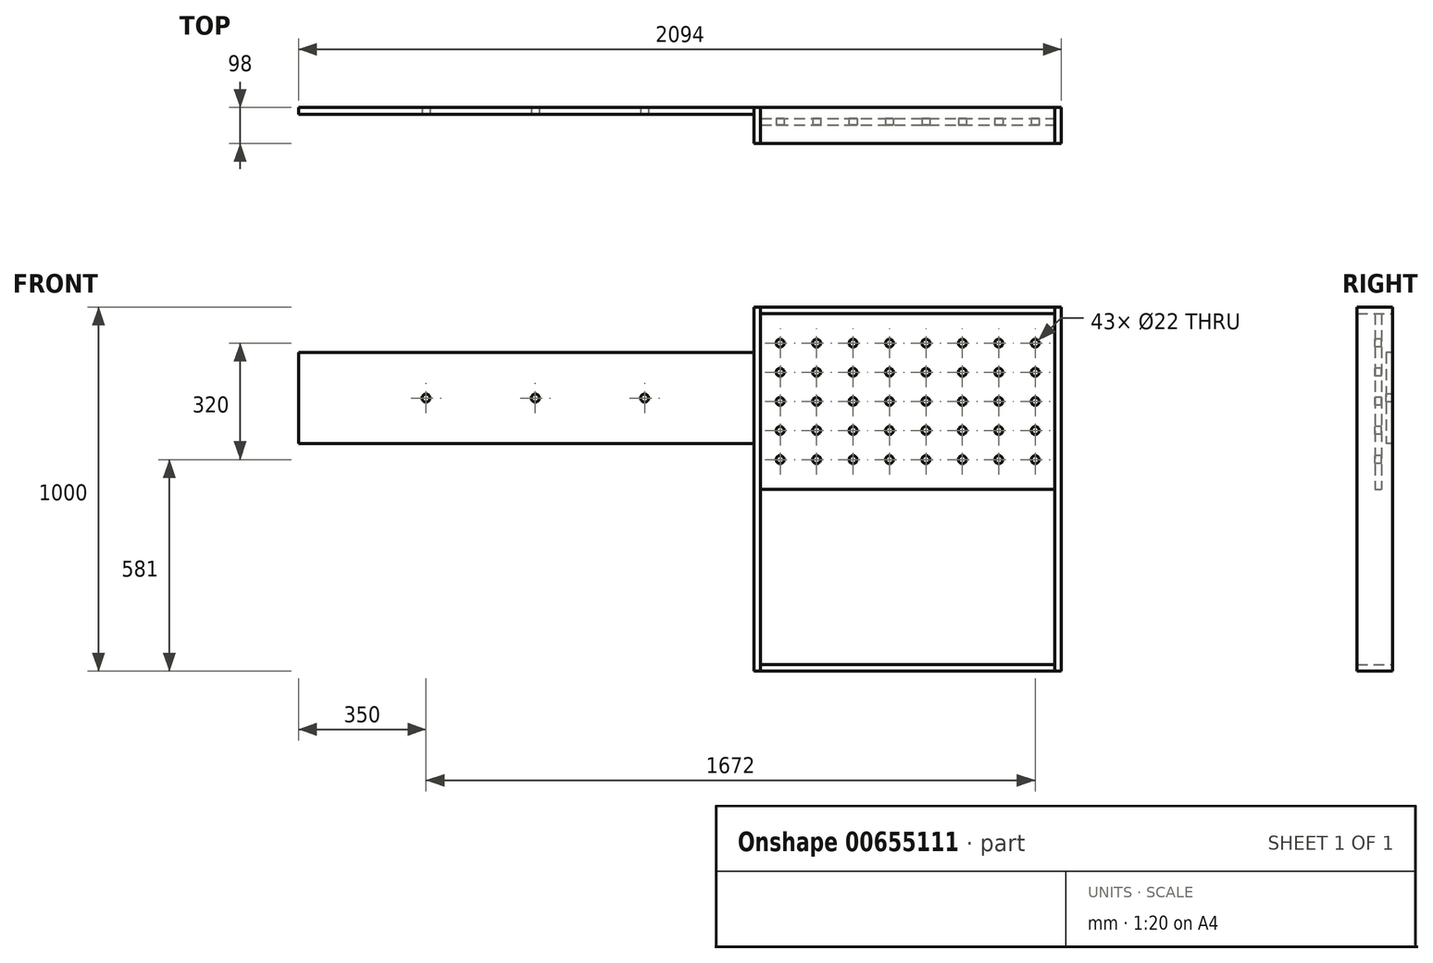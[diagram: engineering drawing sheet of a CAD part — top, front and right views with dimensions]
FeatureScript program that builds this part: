
annotation { "Feature Type Name" : "Feature", "Feature Type Description" : "" }
export const myFeature = defineFeature(function(context is Context, id is Id, definition is map)
    precondition{}
    {
        {
            var Q0;
            Q0=qCreatedBy(makeId("Front.planeOp"),FACE);
            var sketch = newSketch(context, id + "F0", { "sketchPlane" : qUnion([Q0])});
            skLineSegment(sketch, "E0.bottom", {"start": v(-404, 241) * mm, "end": v(404, 241) * mm});
            skLineSegment(sketch, "E0.top", {"start": v(-404, -241) * mm, "end": v(404, -241) * mm});
            skLineSegment(sketch, "E0.left", {"start": v(-404, 241) * mm, "end": v(-404, -241) * mm});
            skLineSegment(sketch, "E0.right", {"start": v(404, 241) * mm, "end": v(404, -241) * mm});
            skPoint(sketch, "E0.middle", {"position": v(0, 0) * mm});
            skSolve(sketch);
        }
        {
            var Q0;
            Q0 = qSketchRegion(id + "F0", true);
            extrude(context, id + "F1", {"entities" : qUnion([Q0]), "depth" : 18 * mm, "offsetDistance" : 25 * mm});
        }
        {
            var Q0;
            Q0=makeQuery(id+"F1.opExtrude","CAP_FACE",FACE,{"disambiguationData":[OSD([sQuery(id+"F0.wireOp",EDGE,"E0.bottom"),sQuery(id+"F0.wireOp",EDGE,"E0.top"),sQuery(id+"F0.wireOp",EDGE,"E0.left"),sQuery(id+"F0.wireOp",EDGE,"E0.right")])],"isStart":false});
            var sketch = newSketch(context, id + "F2", { "sketchPlane" : qUnion([Q0])});
            skLineSegment(sketch, "E1.bottom", {"start": v(-404, 241) * mm, "end": v(404, 241) * mm});
            skLineSegment(sketch, "E1.top", {"start": v(-404, 259) * mm, "end": v(404, 259) * mm});
            skLineSegment(sketch, "E1.left", {"start": v(-404, 241) * mm, "end": v(-404, 259) * mm});
            skLineSegment(sketch, "E1.right", {"start": v(404, 241) * mm, "end": v(404, 259) * mm});
            skLineSegment(sketch, "E2.bottom", {"start": v(-404, -723) * mm, "end": v(404, -723) * mm});
            skLineSegment(sketch, "E2.top", {"start": v(-404, -741) * mm, "end": v(404, -741) * mm});
            skLineSegment(sketch, "E2.left", {"start": v(-404, -723) * mm, "end": v(-404, -741) * mm});
            skLineSegment(sketch, "E2.right", {"start": v(404, -723) * mm, "end": v(404, -741) * mm});
            skSolve(sketch);
        }
        {
            var Q0;
            Q0 = qSketchRegion(id + "F2", true);
            extrude(context, id + "F3", {"entities" : qUnion([Q0]), "depth" : 50 * mm, "offsetDistance" : 25 * mm, "hasSecondDirection" : true, "secondDirectionOppositeDirection" : true, "secondDirectionDepth" : 48 * mm});
        }
        {
            var Q0;
            Q0=makeQuery(id+"F1.opExtrude","CAP_FACE",FACE,{"disambiguationData":[OSD([sQuery(id+"F0.wireOp",EDGE,"E0.bottom"),sQuery(id+"F0.wireOp",EDGE,"E0.top"),sQuery(id+"F0.wireOp",EDGE,"E0.left"),sQuery(id+"F0.wireOp",EDGE,"E0.right")])],"isStart":false});
            var sketch = newSketch(context, id + "F4", { "sketchPlane" : qUnion([Q0])});
            skLineSegment(sketch, "E3.bottom", {"start": v(404, -741) * mm, "end": v(422, -741) * mm});
            skLineSegment(sketch, "E3.top", {"start": v(404, 259) * mm, "end": v(422, 259) * mm});
            skLineSegment(sketch, "E3.left", {"start": v(404, -741) * mm, "end": v(404, 259) * mm});
            skLineSegment(sketch, "E3.right", {"start": v(422, -741) * mm, "end": v(422, 259) * mm});
            skLineSegment(sketch, "E4.bottom", {"start": v(-404, -741) * mm, "end": v(-422, -741) * mm});
            skLineSegment(sketch, "E4.top", {"start": v(-404, 259) * mm, "end": v(-422, 259) * mm});
            skLineSegment(sketch, "E4.left", {"start": v(-404, -741) * mm, "end": v(-404, 259) * mm});
            skLineSegment(sketch, "E4.right", {"start": v(-422, -741) * mm, "end": v(-422, 259) * mm});
            skSolve(sketch);
        }
        {
            var Q0;
            Q0 = qSketchRegion(id + "F4", true);
            extrude(context, id + "F5", {"entities" : qUnion([Q0]), "depth" : 50 * mm, "offsetDistance" : 25 * mm, "hasSecondDirection" : true, "secondDirectionOppositeDirection" : true, "secondDirectionDepth" : 48 * mm});
        }
        {
            var Q0;
            {var subQ1=makeQuery(id+"F1.opExtrude","CAP_EDGE",EDGE,{"disambiguationData":[OSD([sQuery(id+"F0.wireOp",EDGE,"E0.bottom")])],"isStart":false});Q0=makeQuery(id+"F4.imprint","IMPRINT",FACE,{"disambiguationData":[TD([[makeQuery(id+"F4.imprint","IMPRINT",EDGE,{"derivedFrom":subQ1}),-1.0]])]});}
            var sketch = newSketch(context, id + "F6", { "sketchPlane" : qUnion([Q0])});
            skCircle(sketch, "E5", {"center": v(-350, 160) * mm, "radius": 11 * mm});
            skCircle(sketch, "E6.0.1.0", {"center": v(-350, 80) * mm, "radius": 11 * mm});
            skCircle(sketch, "E6.0.2.0", {"center": v(-350, 0) * mm, "radius": 11 * mm});
            skCircle(sketch, "E6.0.3.0", {"center": v(-350, -80) * mm, "radius": 11 * mm});
            skCircle(sketch, "E6.0.4.0", {"center": v(-350, -160) * mm, "radius": 11 * mm});
            skCircle(sketch, "E6.1.0.0", {"center": v(-250, 160) * mm, "radius": 11 * mm});
            skCircle(sketch, "E6.1.1.0", {"center": v(-250, 80) * mm, "radius": 11 * mm});
            skCircle(sketch, "E6.1.2.0", {"center": v(-250, 0) * mm, "radius": 11 * mm});
            skCircle(sketch, "E6.1.3.0", {"center": v(-250, -80) * mm, "radius": 11 * mm});
            skCircle(sketch, "E6.1.4.0", {"center": v(-250, -160) * mm, "radius": 11 * mm});
            skCircle(sketch, "E6.2.0.0", {"center": v(-150, 160) * mm, "radius": 11 * mm});
            skCircle(sketch, "E6.2.1.0", {"center": v(-150, 80) * mm, "radius": 11 * mm});
            skCircle(sketch, "E6.2.2.0", {"center": v(-150, 0) * mm, "radius": 11 * mm});
            skCircle(sketch, "E6.2.3.0", {"center": v(-150, -80) * mm, "radius": 11 * mm});
            skCircle(sketch, "E6.2.4.0", {"center": v(-150, -160) * mm, "radius": 11 * mm});
            skCircle(sketch, "E6.3.0.0", {"center": v(-50, 160) * mm, "radius": 11 * mm});
            skCircle(sketch, "E6.3.1.0", {"center": v(-50, 80) * mm, "radius": 11 * mm});
            skCircle(sketch, "E6.3.2.0", {"center": v(-50, 0) * mm, "radius": 11 * mm});
            skCircle(sketch, "E6.3.3.0", {"center": v(-50, -80) * mm, "radius": 11 * mm});
            skCircle(sketch, "E6.3.4.0", {"center": v(-50, -160) * mm, "radius": 11 * mm});
            skCircle(sketch, "E6.4.0.0", {"center": v(50, 160) * mm, "radius": 11 * mm});
            skCircle(sketch, "E6.4.1.0", {"center": v(50, 80) * mm, "radius": 11 * mm});
            skCircle(sketch, "E6.4.2.0", {"center": v(50, 0) * mm, "radius": 11 * mm});
            skCircle(sketch, "E6.4.3.0", {"center": v(50, -80) * mm, "radius": 11 * mm});
            skCircle(sketch, "E6.4.4.0", {"center": v(50, -160) * mm, "radius": 11 * mm});
            skCircle(sketch, "E6.5.0.0", {"center": v(150, 160) * mm, "radius": 11 * mm});
            skCircle(sketch, "E6.5.1.0", {"center": v(150, 80) * mm, "radius": 11 * mm});
            skCircle(sketch, "E6.5.2.0", {"center": v(150, 0) * mm, "radius": 11 * mm});
            skCircle(sketch, "E6.5.3.0", {"center": v(150, -80) * mm, "radius": 11 * mm});
            skCircle(sketch, "E6.5.4.0", {"center": v(150, -160) * mm, "radius": 11 * mm});
            skCircle(sketch, "E6.6.0.0", {"center": v(250, 160) * mm, "radius": 11 * mm});
            skCircle(sketch, "E6.6.1.0", {"center": v(250, 80) * mm, "radius": 11 * mm});
            skCircle(sketch, "E6.6.2.0", {"center": v(250, 0) * mm, "radius": 11 * mm});
            skCircle(sketch, "E6.6.3.0", {"center": v(250, -80) * mm, "radius": 11 * mm});
            skCircle(sketch, "E6.6.4.0", {"center": v(250, -160) * mm, "radius": 11 * mm});
            skCircle(sketch, "E6.7.0.0", {"center": v(350, 160) * mm, "radius": 11 * mm});
            skCircle(sketch, "E6.7.1.0", {"center": v(350, 80) * mm, "radius": 11 * mm});
            skCircle(sketch, "E6.7.2.0", {"center": v(350, 0) * mm, "radius": 11 * mm});
            skCircle(sketch, "E6.7.3.0", {"center": v(350, -80) * mm, "radius": 11 * mm});
            skCircle(sketch, "E6.7.4.0", {"center": v(350, -160) * mm, "radius": 11 * mm});
            skLineSegment(sketch, "E6.direction1", {"start": v(-350, 160) * mm, "end": v(-250, 160) * mm, "construction": true});
            skLineSegment(sketch, "E6.direction2", {"start": v(-350, 160) * mm, "end": v(-350, 80) * mm, "construction": true});
            skLineSegment(sketch, "E7", {"start": v(0, 0) * mm, "end": v(422.1, 0) * mm, "construction": true});
            skLineSegment(sketch, "E8", {"start": v(0, 241) * mm, "end": v(0, -241) * mm, "construction": true});
            skSolve(sketch);
        }
        {
            var Q0;
            Q0 = qSketchRegion(id + "F6", true);
            extrude(context, id + "F7", {"entities" : qUnion([Q0]), "operationType" : NewBodyOperationType.REMOVE, "endBound" : BoundingType.THROUGH_ALL, "oppositeDirection" : true, "depth" : 25 * mm, "offsetDistance" : 25 * mm});
        }
        {
            var Q0;
            Q0=makeQuery(id+"F5.opExtrude","SWEPT_FACE",FACE,{"disambiguationData":[OSD([sQuery(id+"F4.wireOp",EDGE,"E4.right")])]});
            var sketch = newSketch(context, id + "F8", { "sketchPlane" : qUnion([Q0])});
            skLineSegment(sketch, "E9.bottom", {"start": v(-30, 134) * mm, "end": v(-12, 134) * mm});
            skLineSegment(sketch, "E9.top", {"start": v(-30, -116) * mm, "end": v(-12, -116) * mm});
            skLineSegment(sketch, "E9.left", {"start": v(-30, 134) * mm, "end": v(-30, -116) * mm});
            skLineSegment(sketch, "E9.right", {"start": v(-12, 134) * mm, "end": v(-12, -116) * mm});
            skSolve(sketch);
        }
        {
            var Q0;
            Q0 = qSketchRegion(id + "F8", true);
            extrude(context, id + "F9", {"entities" : qUnion([Q0]), "depth" : 1250 * mm, "offsetDistance" : 25 * mm});
        }
        {
            var Q0;
            Q0=makeQuery(id+"F9.opExtrude","SWEPT_FACE",FACE,{"disambiguationData":[OSD([sQuery(id+"F8.wireOp",EDGE,"E9.right")])]});
            var sketch = newSketch(context, id + "F10", { "sketchPlane" : qUnion([Q0])});
            skLineSegment(sketch, "E10", {"start": v(-1672, 9) * mm, "end": v(-422, 9) * mm, "construction": true});
            skCircle(sketch, "E11", {"center": v(-722, 9) * mm, "radius": 11 * mm});
            skCircle(sketch, "E12.1.0.0", {"center": v(-1022, 9) * mm, "radius": 11 * mm});
            skCircle(sketch, "E12.2.0.0", {"center": v(-1322, 9) * mm, "radius": 11 * mm});
            skLineSegment(sketch, "E12.direction1", {"start": v(-722, 9) * mm, "end": v(-1022, 9) * mm, "construction": true});
            skSolve(sketch);
        }
        {
            var Q0;
            Q0 = qSketchRegion(id + "F10", true);
            extrude(context, id + "F11", {"entities" : qUnion([Q0]), "operationType" : NewBodyOperationType.REMOVE, "oppositeDirection" : true, "depth" : 25 * mm, "offsetDistance" : 25 * mm});
        }
    });
